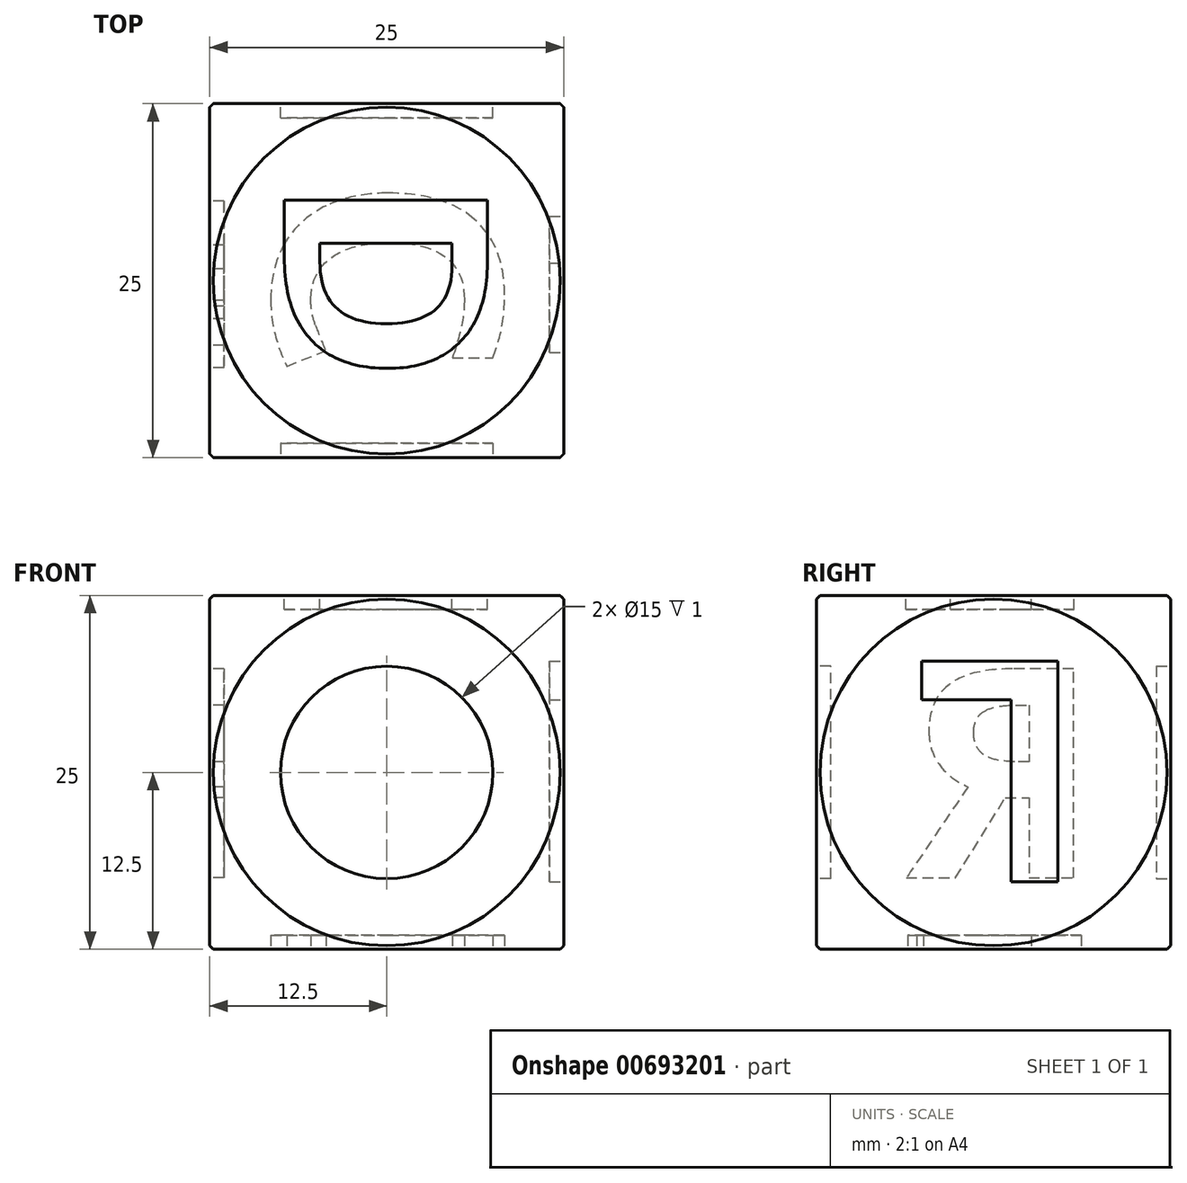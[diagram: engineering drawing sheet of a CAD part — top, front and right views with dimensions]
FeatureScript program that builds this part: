
annotation { "Feature Type Name" : "Feature", "Feature Type Description" : "" }
export const myFeature = defineFeature(function(context is Context, id is Id, definition is map)
    precondition{}
    {
        {
            var Q0;
            Q0=qCreatedBy(makeId("Top.planeOp"),FACE);
            var sketch = newSketch(context, id + "F0", { "sketchPlane" : qUnion([Q0])});
            skLineSegment(sketch, "E0.bottom", {"start": v(12.5, 12.5) * mm, "end": v(-12.5, 12.5) * mm});
            skLineSegment(sketch, "E0.top", {"start": v(12.5, -12.5) * mm, "end": v(-12.5, -12.5) * mm});
            skLineSegment(sketch, "E0.left", {"start": v(12.5, 12.5) * mm, "end": v(12.5, -12.5) * mm});
            skLineSegment(sketch, "E0.right", {"start": v(-12.5, 12.5) * mm, "end": v(-12.5, -12.5) * mm});
            skPoint(sketch, "E0.middle", {"position": v(0, 0) * mm});
            skSolve(sketch);
        }
        {
            var Q0;
            Q0=makeQuery(id+"F0.imprint","IMPRINT",FACE,{"disambiguationData":[TD([[makeQuery(id+"F0.imprint","IMPRINT",EDGE,{"derivedFrom":sQuery(id+"F0.wireOp",EDGE,"E0.bottom")}),1.0]])]});
            extrude(context, id + "F1", {"entities" : qUnion([Q0]), "depth" : 25 * mm, "offsetDistance" : 25 * mm});
        }
        {
            var Q0;
            Q0=makeQuery(id+"F1.opExtrude","CAP_FACE",FACE,{"disambiguationData":[OSD([sQuery(id+"F0.wireOp",EDGE,"E0.bottom"),sQuery(id+"F0.wireOp",EDGE,"E0.top"),sQuery(id+"F0.wireOp",EDGE,"E0.left"),sQuery(id+"F0.wireOp",EDGE,"E0.right")])],"isStart":false});
            var sketch = newSketch(context, id + "F2", { "sketchPlane" : qUnion([Q0])});
            skText(sketch, "E1", { "text": "D", "fontName": "OpenSans-Bold.ttf"});
            skLineSegment(sketch, "E2", {"start": v(7.23, 0) * mm, "end": v(12.5, 0) * mm, "construction": true});
            skLineSegment(sketch, "E3", {"start": v(-7.23, 0) * mm, "end": v(-12.5, 0) * mm, "construction": true});
            const initialGuessF2  = {"E1": [-0.00723, 0.0075, 0, -1, 0.01446]};
            skSetInitialGuess(sketch, initialGuessF2);
            skSolve(sketch);
        }
        {
            var Q0;
            Q0=makeQuery(id+"F2.imprint","IMPRINT",FACE,{"disambiguationData":[TD([[makeQuery(id+"F2.imprint","IMPRINT",EDGE,{"derivedFrom":sQuery(id+"F2.wireOp",EDGE,"E1.sketch_text.stroke-0")}),-1.0]])]});
            extrude(context, id + "F3", {"entities" : qUnion([Q0]), "operationType" : NewBodyOperationType.REMOVE, "oppositeDirection" : true, "depth" : 1 * mm, "offsetDistance" : 25 * mm});
        }
        {
            var Q0;
            Q0=makeQuery(id+"F1.opExtrude","SWEPT_FACE",FACE,{"disambiguationData":[OSD([sQuery(id+"F0.wireOp",EDGE,"E0.top")])]});
            var sketch = newSketch(context, id + "F4", { "sketchPlane" : qUnion([Q0])});
            skCircle(sketch, "E4", {"center": v(0, 12.5) * mm, "radius": 7.5 * mm});
            skPoint(sketch, "E4.centerSnap0", {"position": v(-12.5, 12.5) * mm});
            skSolve(sketch);
        }
        {
            var Q0;
            Q0=makeQuery(id+"F4.imprint","IMPRINT",FACE,{"disambiguationData":[TD([[makeQuery(id+"F4.imprint","IMPRINT",EDGE,{"derivedFrom":sQuery(id+"F4.wireOp",EDGE,"E4")}),1.0]])]});
            extrude(context, id + "F5", {"entities" : qUnion([Q0]), "operationType" : NewBodyOperationType.REMOVE, "oppositeDirection" : true, "depth" : 1 * mm, "offsetDistance" : 25 * mm});
        }
        {
            var Q0;
            Q0=makeQuery(id+"F1.opExtrude","SWEPT_FACE",FACE,{"disambiguationData":[OSD([sQuery(id+"F0.wireOp",EDGE,"E0.bottom")])]});
            var sketch = newSketch(context, id + "F6", { "sketchPlane" : qUnion([Q0])});
            skCircle(sketch, "E5", {"center": v(0, 12.5) * mm, "radius": 7.5 * mm});
            skPoint(sketch, "E5.centerSnap0", {"position": v(12.5, 12.5) * mm});
            skSolve(sketch);
        }
        {
            var Q0;
            Q0=makeQuery(id+"F6.imprint","IMPRINT",FACE,{"disambiguationData":[TD([[makeQuery(id+"F6.imprint","IMPRINT",EDGE,{"derivedFrom":sQuery(id+"F6.wireOp",EDGE,"E5")}),1.0]])]});
            extrude(context, id + "F7", {"entities" : qUnion([Q0]), "operationType" : NewBodyOperationType.REMOVE, "oppositeDirection" : true, "depth" : 1 * mm, "offsetDistance" : 25 * mm});
        }
        {
            var Q0;
            Q0=makeQuery(id+"F1.opExtrude","SWEPT_FACE",FACE,{"disambiguationData":[OSD([sQuery(id+"F0.wireOp",EDGE,"E0.left")])]});
            var sketch = newSketch(context, id + "F8", { "sketchPlane" : qUnion([Q0])});
            skText(sketch, "E6", { "text": "L", "fontName": "OpenSans-Bold.ttf"});
            skLineSegment(sketch, "E7", {"start": v(0, 20.36) * mm, "end": v(0, 25) * mm, "construction": true});
            skLineSegment(sketch, "E8", {"start": v(0, 4.64) * mm, "end": v(0, 0) * mm, "construction": true});
            const initialGuessF8  = {"E6": [0.0065, 0.02036, -1, 0, 0.01571]};
            skSetInitialGuess(sketch, initialGuessF8);
            skSolve(sketch);
        }
        {
            var Q0;
            Q0=makeQuery(id+"F8.imprint","IMPRINT",FACE,{"disambiguationData":[TD([[makeQuery(id+"F8.imprint","IMPRINT",EDGE,{"derivedFrom":sQuery(id+"F8.wireOp",EDGE,"E6.sketch_text.stroke-0")}),-1.0]])]});
            extrude(context, id + "F9", {"entities" : qUnion([Q0]), "operationType" : NewBodyOperationType.REMOVE, "oppositeDirection" : true, "depth" : 1 * mm, "offsetDistance" : 25 * mm});
        }
        {
            var Q0;
            Q0=makeQuery(id+"F1.opExtrude","SWEPT_FACE",FACE,{"disambiguationData":[OSD([sQuery(id+"F0.wireOp",EDGE,"E0.right")])]});
            var sketch = newSketch(context, id + "F10", { "sketchPlane" : qUnion([Q0])});
            skText(sketch, "E9", { "text": "R", "fontName": "OpenSans-Bold.ttf"});
            skLineSegment(sketch, "E10", {"start": v(0, 25) * mm, "end": v(0, 19.95) * mm, "construction": true});
            skLineSegment(sketch, "E11", {"start": v(0, 5.05) * mm, "end": v(0, 0) * mm, "construction": true});
            const initialGuessF10  = {"E9": [-0.0075, 0.00505, 1, 0, 0.0149]};
            skSetInitialGuess(sketch, initialGuessF10);
            skSolve(sketch);
        }
        {
            var Q0;
            Q0=makeQuery(id+"F10.imprint","IMPRINT",FACE,{"disambiguationData":[TD([[makeQuery(id+"F10.imprint","IMPRINT",EDGE,{"derivedFrom":sQuery(id+"F10.wireOp",EDGE,"E9.sketch_text.stroke-0")}),-1.0]])]});
            extrude(context, id + "F11", {"entities" : qUnion([Q0]), "operationType" : NewBodyOperationType.REMOVE, "oppositeDirection" : true, "depth" : 1 * mm, "offsetDistance" : 25 * mm});
        }
        {
            var Q0;
            Q0=makeQuery(id+"F1.opExtrude","CAP_FACE",FACE,{"disambiguationData":[OSD([sQuery(id+"F0.wireOp",EDGE,"E0.bottom"),sQuery(id+"F0.wireOp",EDGE,"E0.top"),sQuery(id+"F0.wireOp",EDGE,"E0.left"),sQuery(id+"F0.wireOp",EDGE,"E0.right")])],"isStart":true});
            var sketch = newSketch(context, id + "F12", { "sketchPlane" : qUnion([Q0])});
            skText(sketch, "E12", { "text": "C", "fontName": "OpenSans-Bold.ttf"});
            skLineSegment(sketch, "E13", {"start": v(-8.1, 0) * mm, "end": v(-12.5, 0) * mm, "construction": true});
            skLineSegment(sketch, "E14", {"start": v(8.1, 0) * mm, "end": v(12.5, 0) * mm, "construction": true});
            const initialGuessF12  = {"E12": [0.0081, -0.0075, 0, 1, 0.0162]};
            skSetInitialGuess(sketch, initialGuessF12);
            skSolve(sketch);
        }
        {
            var Q0;
            Q0=makeQuery(id+"F12.imprint","IMPRINT",FACE,{"disambiguationData":[TD([[makeQuery(id+"F12.imprint","IMPRINT",EDGE,{"derivedFrom":sQuery(id+"F12.wireOp",EDGE,"E12.sketch_text.stroke-0")}),-1.0]])]});
            extrude(context, id + "F13", {"entities" : qUnion([Q0]), "operationType" : NewBodyOperationType.REMOVE, "oppositeDirection" : true, "depth" : 1 * mm, "offsetDistance" : 25 * mm});
        }
        {
            var Q0;
            Q0=qCreatedBy(makeId("Right.planeOp"),FACE);
            var sketch = newSketch(context, id + "F14", { "sketchPlane" : qUnion([Q0])});
            skCircle(sketch, "E15", {"center": v(0, 12.5) * mm, "radius": 17.5 * mm});
            skLineSegment(sketch, "E16", {"start": v(0, 30) * mm, "end": v(0, -5) * mm});
            skSolve(sketch);
        }
        {
            var Q0;
            {var subQ0=sQuery(id+"F14.wireOp",EDGE,"E16");Q0=makeQuery(id+"F14.imprint","IMPRINT",FACE,{"disambiguationData":[TD([[makeQuery(id+"F14.imprint","IMPRINT",EDGE,{"derivedFrom":subQ0}),-1.0]])]});}
            var Q1;
            Q1=sQuery(id+"F14.wireOp",EDGE,"E16");
            revolve(context, id + "F15", {"operationType" : NewBodyOperationType.INTERSECT, "entities" : qUnion([Q0]), "axis" : qUnion([Q1]), "revolveType" : RevolveType.FULL, "oppositeDirection" : true});
        }
    });
